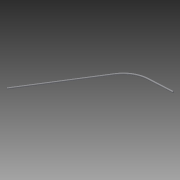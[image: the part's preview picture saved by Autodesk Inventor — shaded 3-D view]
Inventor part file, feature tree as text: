
AUTODESK INVENTOR PART (.ipt)
format: ipt  version: 2013 (Build 170138000, 138)  size: 102,400 bytes
history: native  units: in
note: dims shown in document units (in); Inventor stores cm internally (conversion verified against a paired STEP export)
features: sketch x2, sweep x1
ambient origin geometry x8: Origin, YZ Plane, XZ Plane, XY Plane, X Axis, Y Axis, Z Axis, Center Point
bodies: Solid1 (feature_tree)
feature tree (3):
  sweep  "Sweep1"
  sketch  "Sketch3"  dims[d4=0.5in d6=0.0in]
  sketch  "Sketch5"  dims[d7=32.0in d8=22.0in d9=6.0in d14=60.0in d15=24.0in d16=16.0in d17=8.9443in d20=17.888in d21=24.0in d24=45.0deg d25=44.798in d26=8.944in d27=0.8603in d29=0.5452in d31=25.0711in d32=17.8885in d48=26.5358in d49=8.0003in d50=22.399in]
